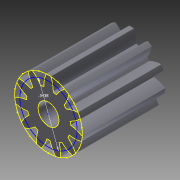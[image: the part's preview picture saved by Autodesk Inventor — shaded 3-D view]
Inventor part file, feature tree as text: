
AUTODESK INVENTOR PART (.ipt)
format: ipt  version: 2012 (Build 160160000, 160)  size: 262,144 bytes
history: native  units: mm (DEFAULTED — no unit token found)
features: sketch x6, plane x3, other x3, extrude x2
ambient origin geometry x8: Origin, YZ Plane, XZ Plane, XY Plane, X Axis, Y Axis, Z Axis, Center Point
bodies: Solid1 (feature_tree)
feature tree (14):
  extrude  "Extrusion1"  Depth=12.7mm TaperAngle=0.0deg
  plane  "Work Plane1"
  plane  "Work Plane2"
  plane  "Work Plane3"
  other  "Spur Gear"
  sketch  "Sketch3"  dims[d6=0.0mm d7=2.855993mm]
  sketch  "Sketch4"  dims[d20=3.19278mm]
  extrude  "Extrusion2"  Depth=76.2mm TaperAngle=0.0deg
  sketch  "Sketch6"  dims[d23=8.73252mm]
  sketch  "Sketch1"  dims[d0=10.31875mm d1=12.7mm d2=0.0mm]
  sketch  "Sketch2"  dims[d3=8.73125mm d4=76.2mm d5=0.0mm]
  other  "Srf1"
  sketch  "Sketch5"  dims[d21=12.7mm d22=0.0mm]
  other  "Pitch Diameter"
